# Revit family: LightHAWK2
name_source: partatom
category: Communication Devices
units: mm (PartAtom-declared; Revit-internal decimal feet)

## family parameters
Cut with Voids When Loaded = No
Host = Face
Maintain Annotation Orientation = No
OmniClass Number = 23.85.80.11.27
OmniClass Title = Lighting Controls
Part Type = Normal
Room Calculation Point = No
Round Connector Dimension = Use Diameter
Shared = Yes

## types (1)
- LightHAWK2
    Apparent Load = 0 VA
    Assembly Code = D5090
    Certifications = Listed UL and cUL
    Coverage = 1,000 square-foot, 180° coverage area
    Default Elevation = 48 "
    Description = graphic wall station is an attractive and
capable user interface for a NX controlled space
    Dimming = 0-10V, Sink up to 30mA
    Features = Digital dual technology passive infrared (PIR) and ultrasonic (US) sensor
• IntelliDAPT self-adaptive technology—no manual adjustment required
• 1 relay model for single-level switching
• Occupancy (auto-on) and Vacancy (manual-on) operating modes
• 1,000 square-foot, 180° coverage area
• RhinoTuff™ vandal resistant lens
• 120/277VAC and 347VAC Models
• No minimum load requirement
• Zero Arc Point Switching
    Height = 2.7 "
    Height 2 = 3.38 "
    Housing Material = Paint - Matte White
    Inuput Power = 120/277VAC;50/60Hz
347VAC; 50/60Hz
    Manufacturer = NX Lighting Controls
    Model = LightHAWK 2
    Mounting = Single-gang NEMA-style switch box (standard switch box)
Decorator-style wall plate sold separately
    Sensor = Paint - Matte White
    Type Comments = Dimming Wall Switch Occupancy Sensors
    URL = https://www.currentlighting.com
    Warranty = 5-Years Warranty
    Width = 1.72 "

## geometry (parser evidence)
native form markers: Sweep x2
no freeform markers — native parametric forms only
